# Revit family: BIMSF-SSMA-S-Column
name_source: partatom
category: Structural Columns
revit_build: Autodesk Revit 2016 (Build: 20150220_1215(x64)
units: mm (PartAtom-declared; Revit-internal decimal feet)

## family parameters
Always export as geometry = No
Beam cutback in plan = From geometry
Cut with Voids When Loaded = No
Material for Model Behavior = Steel
Section Shape = C-channel Parallel Flange
Shared = No
Show family pre-cut in plan views = Yes

## types (142) — shared parameters
Model = V2

## per-type parameters (varying)
| type | Return | bf | d | tf |
| 162S125-27 | 0' - 0 3/16" | 0' - 1 1/4" | 0' - 1 5/8" | 0' - 0 1/32" |
| 162S125-30 | 0' - 0 3/16" | 0' - 1 1/4" | 0' - 1 5/8" | 0' - 0 1/32" |
| 162S125-33 | 0' - 0 3/16" | 0' - 1 1/4" | 0' - 1 5/8" | 0' - 0 1/32" |
| 250S125-27 | 0' - 0 3/16" | 0' - 1 1/4" | 0' - 2 1/2" | 0' - 0 1/32" |
| 250S125-30 | 0' - 0 3/16" | 0' - 1 1/4" | 0' - 2 1/2" | 0' - 0 1/32" |
| 250S125-33 | 0' - 0 3/16" | 0' - 1 1/4" | 0' - 2 1/2" | 0' - 0 1/32" |
| 250S125-43 | 0' - 0 3/16" | 0' - 1 1/4" | 0' - 2 1/2" | 0' - 0 1/32" |
| 250S125-54 | 0' - 0 3/16" | 0' - 1 1/4" | 0' - 2 1/2" | 0' - 0 1/16" |
| 250S125-68 | 0' - 0 3/16" | 0' - 1 1/4" | 0' - 2 1/2" | 0' - 0 1/16" |
| 350S125-27 | 0' - 0 3/16" | 0' - 1 1/4" | 0' - 3 1/2" | 0' - 0 1/32" |
| 350S125-30 | 0' - 0 3/16" | 0' - 1 1/4" | 0' - 3 1/2" | 0' - 0 1/32" |
| 350S125-33 | 0' - 0 3/16" | 0' - 1 1/4" | 0' - 3 1/2" | 0' - 0 1/32" |
| 350S125-43 | 0' - 0 3/16" | 0' - 1 1/4" | 0' - 3 1/2" | 0' - 0 1/32" |
| 350S125-54 | 0' - 0 3/16" | 0' - 1 1/4" | 0' - 3 1/2" | 0' - 0 1/16" |
| 350S125-68 | 0' - 0 3/16" | 0' - 1 1/4" | 0' - 3 1/2" | 0' - 0 1/16" |
| 362S125-27 | 0' - 0 3/16" | 0' - 1 1/4" | 0' - 3 5/8" | 0' - 0 1/32" |
| 362S125-30 | 0' - 0 3/16" | 0' - 1 1/4" | 0' - 3 5/8" | 0' - 0 1/32" |
| 362S125-33 | 0' - 0 3/16" | 0' - 1 1/4" | 0' - 3 5/8" | 0' - 0 1/32" |
| 362S125-43 | 0' - 0 3/16" | 0' - 1 1/4" | 0' - 3 5/8" | 0' - 0 1/32" |
| 362S125-54 | 0' - 0 3/16" | 0' - 1 1/4" | 0' - 3 5/8" | 0' - 0 1/16" |
| 362S125-68 | 0' - 0 3/16" | 0' - 1 1/4" | 0' - 3 5/8" | 0' - 0 1/16" |
| 400S125-27 | 0' - 0 3/16" | 0' - 1 1/4" | 0' - 4" | 0' - 0 1/32" |
| 400S125-30 | 0' - 0 3/16" | 0' - 1 1/4" | 0' - 4" | 0' - 0 1/32" |
| 400S125-33 | 0' - 0 3/16" | 0' - 1 1/4" | 0' - 4" | 0' - 0 1/32" |
| 400S125-43 | 0' - 0 3/16" | 0' - 1 1/4" | 0' - 4" | 0' - 0 1/32" |
| 400S125-54 | 0' - 0 3/16" | 0' - 1 1/4" | 0' - 4" | 0' - 0 1/16" |
| 400S125-68 | 0' - 0 3/16" | 0' - 1 1/4" | 0' - 4" | 0' - 0 1/16" |
| 550S125-27 | 0' - 0 3/16" | 0' - 1 1/4" | 0' - 5 1/2" | 0' - 0 1/32" |
| 550S125-30 | 0' - 0 3/16" | 0' - 1 1/4" | 0' - 5 1/2" | 0' - 0 1/32" |
| 550S125-33 | 0' - 0 3/16" | 0' - 1 1/4" | 0' - 5 1/2" | 0' - 0 1/32" |
| 550S125-43 | 0' - 0 3/16" | 0' - 1 1/4" | 0' - 5 1/2" | 0' - 0 1/32" |
| 550S125-54 | 0' - 0 3/16" | 0' - 1 1/4" | 0' - 5 1/2" | 0' - 0 1/16" |
| 550S125-68 | 0' - 0 3/16" | 0' - 1 1/4" | 0' - 5 1/2" | 0' - 0 1/16" |
| 600S125-27 | 0' - 0 3/16" | 0' - 1 1/4" | 0' - 6" | 0' - 0 1/32" |
| 600S125-30 | 0' - 0 3/16" | 0' - 1 1/4" | 0' - 6" | 0' - 0 1/32" |
| 600S125-33 | 0' - 0 3/16" | 0' - 1 1/4" | 0' - 6" | 0' - 0 1/32" |
| 600S125-43 | 0' - 0 3/16" | 0' - 1 1/4" | 0' - 6" | 0' - 0 1/32" |
| 600S125-54 | 0' - 0 3/16" | 0' - 1 1/4" | 0' - 6" | 0' - 0 1/16" |
| 600S125-68 | 0' - 0 3/16" | 0' - 1 1/4" | 0' - 6" | 0' - 0 1/16" |
| 800S125-33 | 0' - 0 3/16" | 0' - 1 1/4" | 0' - 8" | 0' - 0 1/32" |
| 800S125-43 | 0' - 0 3/16" | 0' - 1 1/4" | 0' - 8" | 0' - 0 1/32" |
| 800S125-54 | 0' - 0 3/16" | 0' - 1 1/4" | 0' - 8" | 0' - 0 1/16" |
| 800S125-68 | 0' - 0 3/16" | 0' - 1 1/4" | 0' - 8" | 0' - 0 1/16" |
| 250S137-33 | 0' - 0 3/8" | 0' - 1 3/8" | 0' - 2 1/2" | 0' - 0 1/32" |
| 250S137-43 | 0' - 0 3/8" | 0' - 1 3/8" | 0' - 2 1/2" | 0' - 0 1/32" |
| 250S137-54 | 0' - 0 3/8" | 0' - 1 3/8" | 0' - 2 1/2" | 0' - 0 1/16" |
| 250S137-68 | 0' - 0 3/8" | 0' - 1 3/8" | 0' - 2 1/2" | 0' - 0 1/16" |
| 250S162-33 | 0' - 0 1/2" | 0' - 1 5/8" | 0' - 2 1/2" | 0' - 0 1/32" |
| 250S162-43 | 0' - 0 1/2" | 0' - 1 5/8" | 0' - 2 1/2" | 0' - 0 1/32" |
| 250S162-54 | 0' - 0 1/2" | 0' - 1 5/8" | 0' - 2 1/2" | 0' - 0 1/16" |
| 250S162-68 | 0' - 0 1/2" | 0' - 1 5/8" | 0' - 2 1/2" | 0' - 0 1/16" |
| 350S162-33 | 0' - 0 1/2" | 0' - 1 5/8" | 0' - 3 1/2" | 0' - 0 1/32" |
| 350S162-43 | 0' - 0 1/2" | 0' - 1 5/8" | 0' - 3 1/2" | 0' - 0 1/32" |
| 350S162-54 | 0' - 0 1/2" | 0' - 1 5/8" | 0' - 3 1/2" | 0' - 0 1/16" |
| 350S162-68 | 0' - 0 1/2" | 0' - 1 5/8" | 0' - 3 1/2" | 0' - 0 1/16" |
| 362S137-33 | 0' - 0 3/8" | 0' - 1 3/8" | 0' - 3 5/8" | 0' - 0 1/32" |
| 362S137-43 | 0' - 0 3/8" | 0' - 1 3/8" | 0' - 3 5/8" | 0' - 0 1/32" |
| 362S137-54 | 0' - 0 3/8" | 0' - 1 3/8" | 0' - 3 5/8" | 0' - 0 1/16" |
| 362S137-68 | 0' - 0 3/8" | 0' - 1 3/8" | 0' - 3 5/8" | 0' - 0 1/16" |
| 362S162-33 | 0' - 0 1/2" | 0' - 1 5/8" | 0' - 3 5/8" | 0' - 0 1/32" |
| 362S162-43 | 0' - 0 1/2" | 0' - 1 5/8" | 0' - 3 5/8" | 0' - 0 1/32" |
| 362S162-54 | 0' - 0 1/2" | 0' - 1 5/8" | 0' - 3 5/8" | 0' - 0 1/16" |
| 362S162-68 | 0' - 0 1/2" | 0' - 1 5/8" | 0' - 3 5/8" | 0' - 0 1/16" |
| 362S200-33 | 0' - 0 5/8" | 0' - 2" | 0' - 3 5/8" | 0' - 0 1/32" |
| 362S200-43 | 0' - 0 5/8" | 0' - 2" | 0' - 3 5/8" | 0' - 0 1/32" |
| 362S200-54 | 0' - 0 5/8" | 0' - 2" | 0' - 3 5/8" | 0' - 0 1/16" |
| 362S200-68 | 0' - 0 5/8" | 0' - 2" | 0' - 3 5/8" | 0' - 0 1/16" |
| 400S137-33 | 0' - 0 3/8" | 0' - 1 3/8" | 0' - 4" | 0' - 0 1/32" |
| 400S137-43 | 0' - 0 3/8" | 0' - 1 3/8" | 0' - 4" | 0' - 0 1/32" |
| 400S137-54 | 0' - 0 3/8" | 0' - 1 3/8" | 0' - 4" | 0' - 0 1/16" |
| 400S137-68 | 0' - 0 3/8" | 0' - 1 3/8" | 0' - 4" | 0' - 0 1/16" |
| 400S162-33 | 0' - 0 1/2" | 0' - 1 5/8" | 0' - 4" | 0' - 0 1/32" |
| 400S162-43 | 0' - 0 1/2" | 0' - 1 5/8" | 0' - 4" | 0' - 0 1/32" |
| 400S162-54 | 0' - 0 1/2" | 0' - 1 5/8" | 0' - 4" | 0' - 0 1/16" |
| 400S162-68 | 0' - 0 1/2" | 0' - 1 5/8" | 0' - 4" | 0' - 0 1/16" |
| 400S200-33 | 0' - 0 5/8" | 0' - 2" | 0' - 4" | 0' - 0 1/32" |
| 400S200-43 | 0' - 0 5/8" | 0' - 2" | 0' - 4" | 0' - 0 1/32" |
| 400S200-54 | 0' - 0 5/8" | 0' - 2" | 0' - 4" | 0' - 0 1/16" |
| 400S200-68 | 0' - 0 5/8" | 0' - 2" | 0' - 4" | 0' - 0 1/16" |
| 550S162-33 | 0' - 0 1/2" | 0' - 1 5/8" | 0' - 5 1/2" | 0' - 0 1/32" |
| 550S162-43 | 0' - 0 1/2" | 0' - 1 5/8" | 0' - 5 1/2" | 0' - 0 1/32" |
| 550S162-54 | 0' - 0 1/2" | 0' - 1 5/8" | 0' - 5 1/2" | 0' - 0 1/16" |
| 550S162-68 | 0' - 0 1/2" | 0' - 1 5/8" | 0' - 5 1/2" | 0' - 0 1/16" |
| 600S137-33 | 0' - 0 3/8" | 0' - 1 3/8" | 0' - 6" | 0' - 0 1/32" |
| 600S137-43 | 0' - 0 3/8" | 0' - 1 3/8" | 0' - 6" | 0' - 0 1/32" |
| 600S137-54 | 0' - 0 3/8" | 0' - 1 3/8" | 0' - 6" | 0' - 0 1/16" |
| 600S137-68 | 0' - 0 3/8" | 0' - 1 3/8" | 0' - 6" | 0' - 0 1/16" |
| 600S137-97 | 0' - 0 3/8" | 0' - 1 3/8" | 0' - 6" | 0' - 0 3/32" |
| 600S162-33 | 0' - 0 1/2" | 0' - 1 5/8" | 0' - 6" | 0' - 0 1/32" |
| 600S162-43 | 0' - 0 1/2" | 0' - 1 5/8" | 0' - 6" | 0' - 0 1/32" |
| 600S162-54 | 0' - 0 1/2" | 0' - 1 5/8" | 0' - 6" | 0' - 0 1/16" |
| 600S162-68 | 0' - 0 1/2" | 0' - 1 5/8" | 0' - 6" | 0' - 0 1/16" |
| 600S162-97 | 0' - 0 1/2" | 0' - 1 5/8" | 0' - 6" | 0' - 0 3/32" |
| 600S200-33 | 0' - 0 5/8" | 0' - 2" | 0' - 6" | 0' - 0 1/32" |
| 600S200-43 | 0' - 0 5/8" | 0' - 2" | 0' - 6" | 0' - 0 1/32" |
| 600S200-54 | 0' - 0 5/8" | 0' - 2" | 0' - 6" | 0' - 0 1/16" |
| 600S200-68 | 0' - 0 5/8" | 0' - 2" | 0' - 6" | 0' - 0 1/16" |
| 600S200-97 | 0' - 0 5/8" | 0' - 2" | 0' - 6" | 0' - 0 3/32" |
| 600S250-43 | 0' - 0 5/8" | 0' - 2 1/2" | 0' - 6" | 0' - 0 1/32" |
| 600S250-54 | 0' - 0 5/8" | 0' - 2 1/2" | 0' - 6" | 0' - 0 1/16" |
| 600S250-68 | 0' - 0 5/8" | 0' - 2 1/2" | 0' - 6" | 0' - 0 1/16" |
| 600S250-97 | 0' - 0 5/8" | 0' - 2 1/2" | 0' - 6" | 0' - 0 3/32" |
| 800S137-33 | 0' - 0 3/8" | 0' - 1 3/8" | 0' - 8" | 0' - 0 1/32" |
| 800S137-43 | 0' - 0 3/8" | 0' - 1 3/8" | 0' - 8" | 0' - 0 1/32" |
| 800S137-54 | 0' - 0 3/8" | 0' - 1 3/8" | 0' - 8" | 0' - 0 1/16" |
| 800S137-68 | 0' - 0 3/8" | 0' - 1 3/8" | 0' - 8" | 0' - 0 1/16" |
| 800S137-97 | 0' - 0 3/8" | 0' - 1 3/8" | 0' - 8" | 0' - 0 3/32" |
| 800S162-33 | 0' - 0 1/2" | 0' - 1 5/8" | 0' - 8" | 0' - 0 1/32" |
| 800S162-43 | 0' - 0 1/2" | 0' - 1 5/8" | 0' - 8" | 0' - 0 1/32" |
| 800S162-54 | 0' - 0 1/2" | 0' - 1 5/8" | 0' - 8" | 0' - 0 1/16" |
| 800S162-68 | 0' - 0 1/2" | 0' - 1 5/8" | 0' - 8" | 0' - 0 1/16" |
| 800S162-97 | 0' - 0 1/2" | 0' - 1 5/8" | 0' - 8" | 0' - 0 3/32" |
| 800S200-33 | 0' - 0 5/8" | 0' - 2" | 0' - 8" | 0' - 0 1/32" |
| 800S200-43 | 0' - 0 5/8" | 0' - 2" | 0' - 8" | 0' - 0 1/32" |
| 800S200-54 | 0' - 0 5/8" | 0' - 2" | 0' - 8" | 0' - 0 1/16" |
| 800S200-68 | 0' - 0 5/8" | 0' - 2" | 0' - 8" | 0' - 0 1/16" |
| 800S200-97 | 0' - 0 5/8" | 0' - 2" | 0' - 8" | 0' - 0 3/32" |
| 800S250-43 | 0' - 0 5/8" | 0' - 2 1/2" | 0' - 8" | 0' - 0 1/32" |
| 800S250-54 | 0' - 0 5/8" | 0' - 2 1/2" | 0' - 8" | 0' - 0 1/16" |
| 800S250-68 | 0' - 0 5/8" | 0' - 2 1/2" | 0' - 8" | 0' - 0 1/16" |
| 800S250-97 | 0' - 0 5/8" | 0' - 2 1/2" | 0' - 8" | 0' - 0 3/32" |
| 1000S162-43 | 0' - 0 1/2" | 0' - 1 5/8" | 0' - 10" | 0' - 0 1/32" |
| 1000S162-54 | 0' - 0 1/2" | 0' - 1 5/8" | 0' - 10" | 0' - 0 1/16" |
| 1000S162-68 | 0' - 0 1/2" | 0' - 1 5/8" | 0' - 10" | 0' - 0 1/16" |
| 1000S162-97 | 0' - 0 1/2" | 0' - 1 5/8" | 0' - 10" | 0' - 0 3/32" |
| 1000S200-43 | 0' - 0 5/8" | 0' - 2" | 0' - 10" | 0' - 0 1/32" |
| 1000S200-54 | 0' - 0 5/8" | 0' - 2" | 0' - 10" | 0' - 0 1/16" |
| 1000S200-68 | 0' - 0 5/8" | 0' - 2" | 0' - 10" | 0' - 0 1/16" |
| 1000S200-97 | 0' - 0 5/8" | 0' - 2" | 0' - 10" | 0' - 0 3/32" |
| 1000S250-43 | 0' - 0 5/8" | 0' - 2 1/2" | 0' - 10" | 0' - 0 1/32" |
| 1000S250-54 | 0' - 0 5/8" | 0' - 2 1/2" | 0' - 10" | 0' - 0 1/16" |
| 1000S250-68 | 0' - 0 5/8" | 0' - 2 1/2" | 0' - 10" | 0' - 0 1/16" |
| 1000S250-97 | 0' - 0 5/8" | 0' - 2 1/2" | 0' - 10" | 0' - 0 3/32" |
| 1200S162-54 | 0' - 0 1/2" | 0' - 1 5/8" | 1' - 0" | 0' - 0 1/16" |
| 1200S162-68 | 0' - 0 1/2" | 0' - 1 5/8" | 1' - 0" | 0' - 0 1/16" |
| 1200S162-97 | 0' - 0 1/2" | 0' - 1 5/8" | 1' - 0" | 0' - 0 3/32" |
| 1200S200-54 | 0' - 0 5/8" | 0' - 2" | 1' - 0" | 0' - 0 1/16" |
| 1200S200-68 | 0' - 0 5/8" | 0' - 2" | 1' - 0" | 0' - 0 1/16" |
| 1200S200-97 | 0' - 0 5/8" | 0' - 2" | 1' - 0" | 0' - 0 3/32" |
| 1200S250-54 | 0' - 0 5/8" | 0' - 2 1/2" | 1' - 0" | 0' - 0 1/16" |
| 1200S250-68 | 0' - 0 5/8" | 0' - 2 1/2" | 1' - 0" | 0' - 0 1/16" |
| 1200S250-97 | 0' - 0 5/8" | 0' - 2 1/2" | 1' - 0" | 0' - 0 3/32" |

## geometry (parser evidence)
native form markers: Sweep x4
no freeform markers — native parametric forms only
